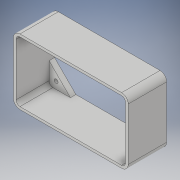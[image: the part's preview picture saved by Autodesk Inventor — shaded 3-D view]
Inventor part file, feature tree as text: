
AUTODESK INVENTOR PART (.ipt)
format: ipt  version: 2018 (Build 220112000, 112)  size: 207,872 bytes
history: native  units: in
note: dims shown in document units (in); Inventor stores cm internally (conversion verified against a paired STEP export)
features: extrude x5, sketch x5, fillet x1
ambient origin geometry x8: Origin, YZ Plane, XZ Plane, XY Plane, X Axis, Y Axis, Z Axis, Center Point
bodies: Solid1 (feature_tree)
feature tree (11):
  extrude  "Extrusion1"  Depth=4.6969in
  fillet  "Fillet1"  Radius=0.3937in
  extrude  "Extrusion3"  Depth=0.4724in
  extrude  "Extrusion4"  Depth=0.6968in
  extrude  "Extrusion5"  Depth=0.4724in
  extrude  "Extrusion7"  Depth=0.3937in TaperAngle=0.0deg
  sketch  "Sketch1"  dims[d0=8.2362in d1=4.6969in d2=0.3937in d3=0.0in]
  sketch  "Sketch3"  dims[d4=0.4724in d16=0.2756in]
  sketch  "Sketch4"  dims[d17=0.7087in d18=0.6968in]
  sketch  "Sketch5"  dims[d19=0.0in d20=0.0in d21=0.4724in]
  sketch  "Sketch8"  dims[d22=0.4724in d23=0.3937in d24=0.0in d25=0.185in d27=4.7802in d30=0.3937in d31=0.0in d37=0.1969in d38=1.2644in d39=0.185in d40=2.3622in d41=0.0in]
